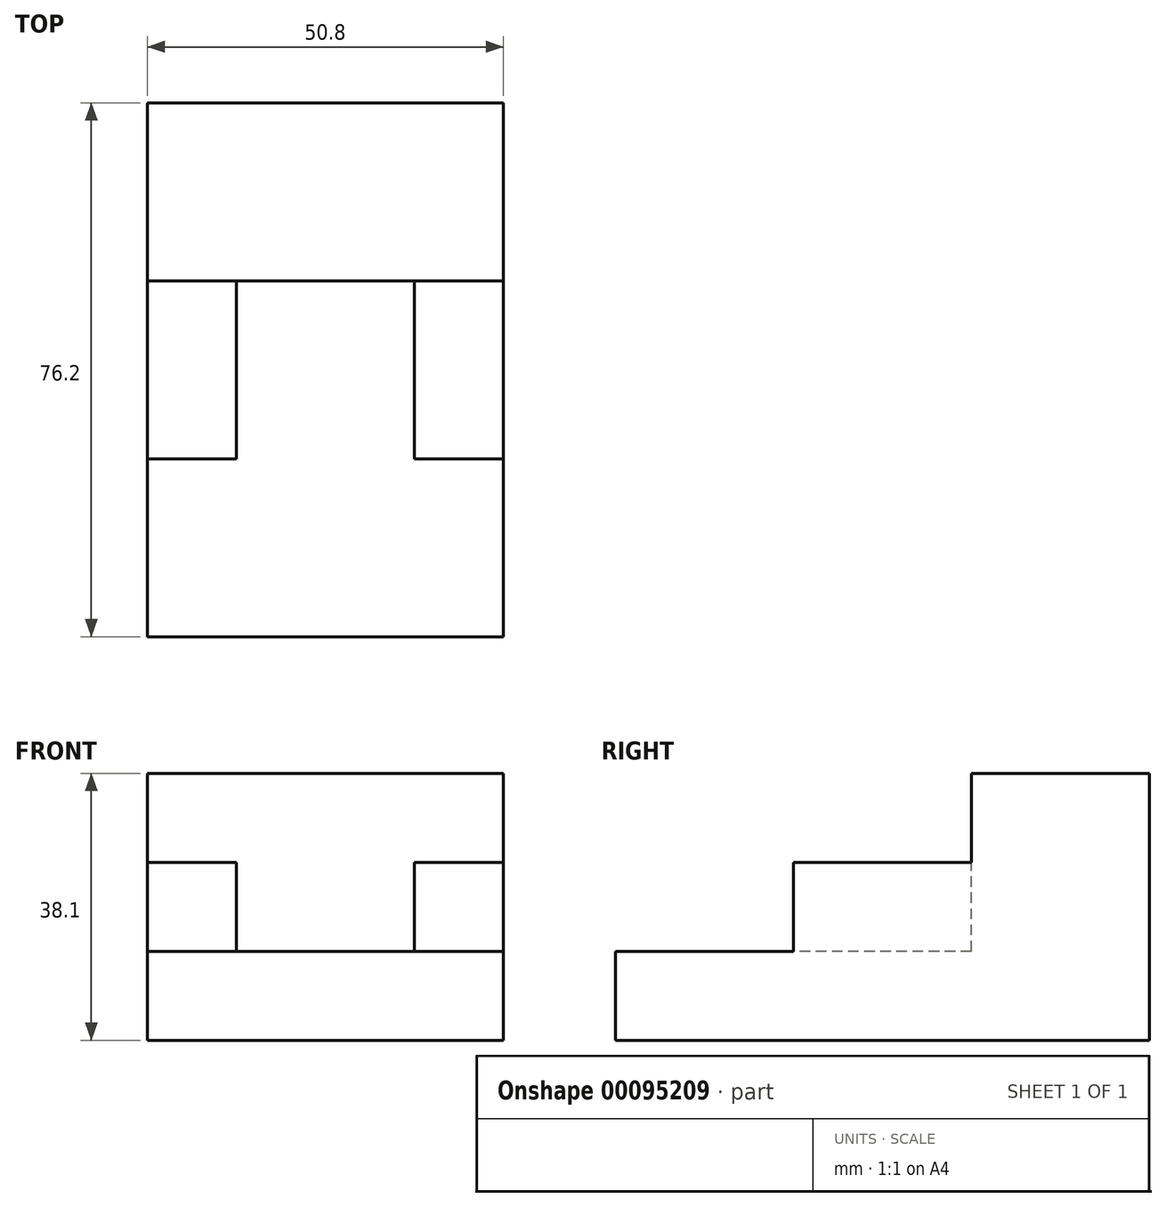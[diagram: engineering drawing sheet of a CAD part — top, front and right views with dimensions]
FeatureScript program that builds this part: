
annotation { "Feature Type Name" : "Feature", "Feature Type Description" : "" }
export const myFeature = defineFeature(function(context is Context, id is Id, definition is map)
    precondition{}
    {
        {
            var Q0;
            Q0=qCreatedBy(makeId("Right.planeOp"),FACE);
            var sketch = newSketch(context, id + "F0", { "sketchPlane" : qUnion([Q0])});
            skLineSegment(sketch, "E0", {"start": v(0, 0) * mm, "end": v(76.2, 0) * mm});
            skLineSegment(sketch, "E1", {"start": v(76.2, 0) * mm, "end": v(76.2, 38.1) * mm});
            skLineSegment(sketch, "E2", {"start": v(76.2, 38.1) * mm, "end": v(50.8, 38.1) * mm});
            skLineSegment(sketch, "E3", {"start": v(50.8, 38.1) * mm, "end": v(50.8, 25.4) * mm});
            skLineSegment(sketch, "E4", {"start": v(50.8, 25.4) * mm, "end": v(25.4, 25.4) * mm});
            skLineSegment(sketch, "E5", {"start": v(25.4, 25.4) * mm, "end": v(25.4, 12.7) * mm});
            skLineSegment(sketch, "E6", {"start": v(25.4, 12.7) * mm, "end": v(0, 12.7) * mm});
            skLineSegment(sketch, "E7", {"start": v(0, 12.7) * mm, "end": v(0, 0) * mm});
            skSolve(sketch);
        }
        {
            var Q0;
            Q0 = qSketchRegion(id + "F0", true);
            extrude(context, id + "F1", {"entities" : qUnion([Q0]), "depth" : 50.8 * mm});
        }
        {
            var Q0;
            Q0=makeQuery(id+"F1.opExtrude","SWEPT_FACE",FACE,{"disambiguationData":[OSD([sQuery(id+"F0.wireOp",EDGE,"E5")])]});
            var sketch = newSketch(context, id + "F2", { "sketchPlane" : qUnion([Q0])});
            skLineSegment(sketch, "E8.bottom", {"start": v(12.7, 12.7) * mm, "end": v(38.1, 12.7) * mm});
            skLineSegment(sketch, "E8.top", {"start": v(12.7, 25.4) * mm, "end": v(38.1, 25.4) * mm});
            skLineSegment(sketch, "E8.left", {"start": v(12.7, 12.7) * mm, "end": v(12.7, 25.4) * mm});
            skLineSegment(sketch, "E8.right", {"start": v(38.1, 12.7) * mm, "end": v(38.1, 25.4) * mm});
            skSolve(sketch);
        }
        {
            var Q0;
            Q0 = qSketchRegion(id + "F2", true);
            var Q1;
            Q1=makeQuery(id+"F1.opExtrude","SWEPT_FACE",FACE,{"disambiguationData":[OSD([sQuery(id+"F0.wireOp",EDGE,"E3")])]});
            extrude(context, id + "F3", {"entities" : qUnion([Q0]), "operationType" : NewBodyOperationType.REMOVE, "endBound" : BoundingType.UP_TO_SURFACE, "oppositeDirection" : true, "endBoundEntityFace" : qUnion([Q1]), "depth" : 25.4 * mm});
        }
    });
